# Revit family: STS-301U Трансляционный аудиоусилитель_RV17_LOD_400 (04.10.23)
name_source: partatom
category: Электрооборудование
revit_build: Autodesk Revit 2017 (Build: 20170118_1100(x64)
units: mm (PartAtom-declared; Revit-internal decimal feet)

## family parameters
Всегда вертикально = Да
Конфигурация панели = Два столбца, слева направо
На основе рабочей плоскости = Нет
Общий = Нет
При загрузке вырезать с полостями = Нет
Размер круглого соединителя = Использовать диаметр
Тип детали = Щит
Точка расчета площади = Нет

## types (1)
- STS-301U
    ADSK_URL страницы изделия = https://stilsoft.ru
    ADSK_Единица измерения = шт.
    ADSK_Завод-изготовитель = ООО «Основа Безопасности»
    ADSK_Количество = 1
    ADSK_Марка = СТАЕ.426469.102
    ADSK_Масса = 4
    ADSK_Наименование = Трансляционный усилитель STS-301U
    ADSK_Размер_Высота = 370 мм
    ADSK_Размер_Глубина = 100 мм
    ADSK_Размер_Ширина = 320 мм
    Датчик вскрытия = имеется
    Диапазон рабочих температур, °С = от +5 до +50
    Количество аудиовыходов для линий оповещения, шт. = 2
    Количество шлейфов сигнализации (ШС), шт. = 4
    Контроль целостности линий до динамиков = имеется
    Максимальное время работы в автономном режиме, не менее, ч = 25
    Максимальное время работы в режиме оповещения, не менее, ч = 1
    Минимальное сопротивление линии оповещения, не менее, Ом = 4
    Мощность = 40
    Мощность аудиовыхода, Вт = 40 Вт
    Мощность встроенного блока питания, Вт = 100
    Напряжение = 220
    Напряжение электропитания в автономном режиме, В = 24 В
    Поддерживаемые протоколы = TCP/IP, UDP/IP, HTTP, RTSP, RTP/UDP
    Поддерживаемые форматы аудио = WAV PCM (без сжатия)
    Подключение к сети = 10 Base-T Ethernet (гнездо RJ-45)
    Потребляемый ток, не более, А = 1 А
    Режим работы = непрерывный
    Резервирование электропитания = имеется
    Сопротивление громкоговорителя, Ом = от 8 до 32
от 8 до 32
    Частота питающего напряжения, Гц = 50 Гц
    частота дискретизации, Гц = 8000, 22050, 32000, 44100
